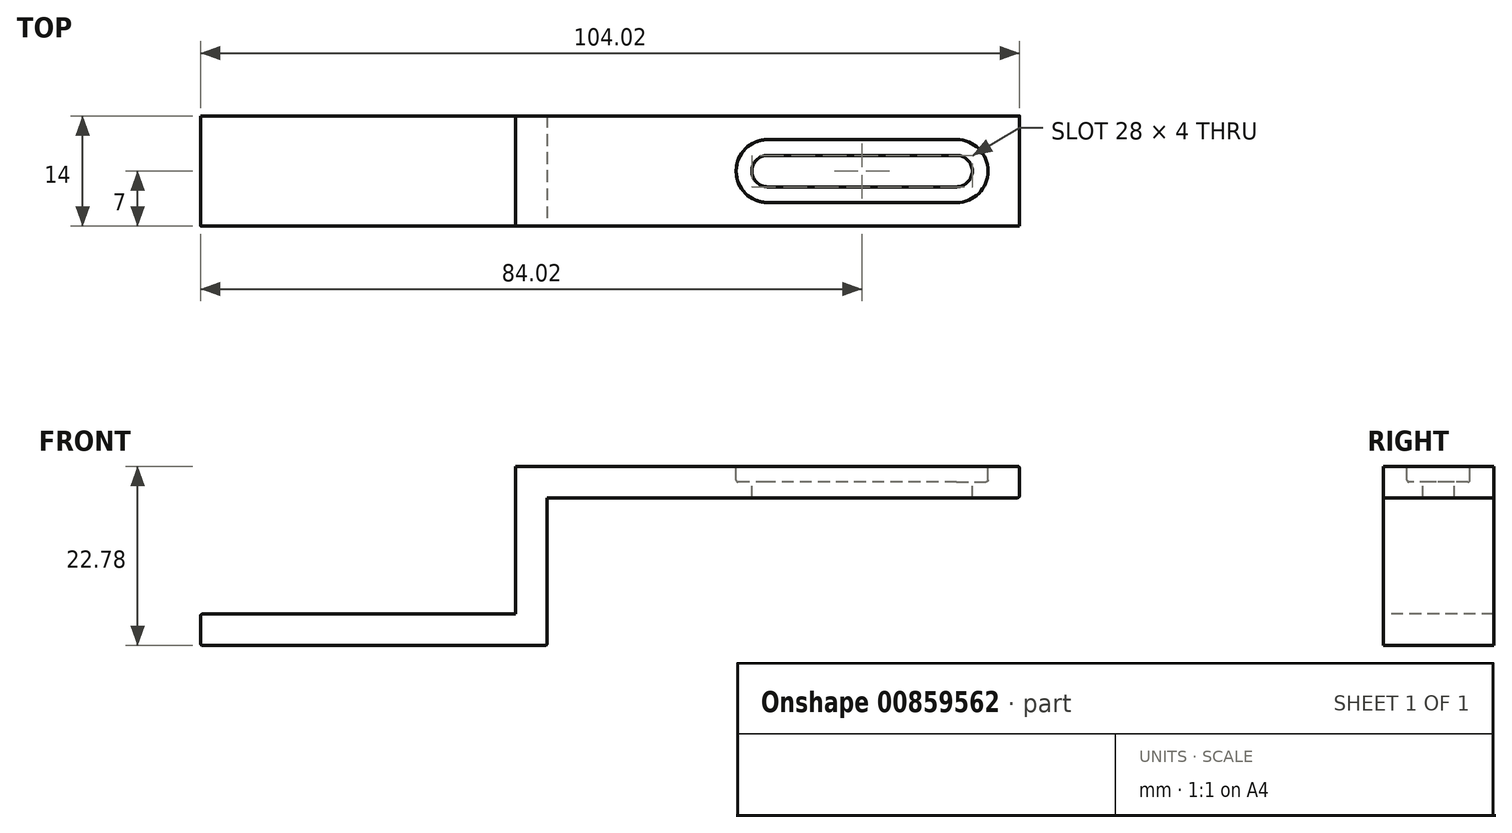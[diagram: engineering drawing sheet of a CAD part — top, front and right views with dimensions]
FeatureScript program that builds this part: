
annotation { "Feature Type Name" : "Feature", "Feature Type Description" : "" }
export const myFeature = defineFeature(function(context is Context, id is Id, definition is map)
    precondition{}
    {
        {
            var Q0;
            Q0=qCreatedBy(makeId("Top.planeOp"),FACE);
            var sketch = newSketch(context, id + "F0", { "sketchPlane" : qUnion([Q0])});
            skLineSegment(sketch, "E0.bottom", {"start": v(43, -7) * mm, "end": v(-43, -7) * mm});
            skLineSegment(sketch, "E0.top", {"start": v(43, 7) * mm, "end": v(-43, 7) * mm});
            skLineSegment(sketch, "E0.left", {"start": v(43, -7) * mm, "end": v(43, 7) * mm});
            skLineSegment(sketch, "E0.right", {"start": v(-43, -7) * mm, "end": v(-43, 7) * mm});
            skPoint(sketch, "E0.middle", {"position": v(0, 0) * mm});
            skSolve(sketch);
        }
        {
            var Q0;
            Q0=qSketchRegion(id+"F0",true);
            extrude(context, id + "F1", {"entities" : qUnion([Q0]), "depth" : 4 * mm, "offsetDistance" : 25.4 * mm});
        }
        {
            var Q0;
            Q0=makeQuery(id+"F1.opExtrude","CAP_FACE",FACE,{"disambiguationData":[OSD([sQuery(id+"F0.wireOp",EDGE,"E0.bottom"),sQuery(id+"F0.wireOp",EDGE,"E0.top"),sQuery(id+"F0.wireOp",EDGE,"E0.left"),sQuery(id+"F0.wireOp",EDGE,"E0.right")])],"isStart":false});
            var sketch = newSketch(context, id + "F2", { "sketchPlane" : qUnion([Q0])});
            skLineSegment(sketch, "E1", {"start": v(-43, 0) * mm, "end": v(43, 0) * mm, "construction": true});
            skCircle(sketch, "E2", {"center": v(35, 0) * mm, "radius": 2 * mm});
            skCircle(sketch, "E3", {"center": v(11, 0) * mm, "radius": 2 * mm});
            skLineSegment(sketch, "E4.bottom", {"start": v(11, -2) * mm, "end": v(35, -2) * mm});
            skLineSegment(sketch, "E4.top", {"start": v(11, 2) * mm, "end": v(35, 2) * mm});
            skLineSegment(sketch, "E4.left", {"start": v(11, -2) * mm, "end": v(11, 2) * mm});
            skLineSegment(sketch, "E4.right", {"start": v(35, -2) * mm, "end": v(35, 2) * mm});
            skSolve(sketch);
        }
        {
            var Q0;
            Q0=qSketchRegion(id+"F2",true);
            extrude(context, id + "F3", {"entities" : qUnion([Q0]), "operationType" : NewBodyOperationType.REMOVE, "oppositeDirection" : true, "depth" : 4 * mm, "offsetDistance" : 25.4 * mm});
        }
        {
            var Q0;
            Q0=makeQuery(id+"F1.opExtrude","CAP_FACE",FACE,{"disambiguationData":[OSD([sQuery(id+"F0.wireOp",EDGE,"E0.bottom"),sQuery(id+"F0.wireOp",EDGE,"E0.top"),sQuery(id+"F0.wireOp",EDGE,"E0.left"),sQuery(id+"F0.wireOp",EDGE,"E0.right")])],"isStart":false});
            var sketch = newSketch(context, id + "F4", { "sketchPlane" : qUnion([Q0])});
            skLineSegment(sketch, "E5", {"start": v(-43, 0) * mm, "end": v(43, 0) * mm, "construction": true});
            skCircle(sketch, "E6", {"center": v(35, 0) * mm, "radius": 4 * mm});
            skCircle(sketch, "E7", {"center": v(11, 0) * mm, "radius": 4 * mm});
            skLineSegment(sketch, "E8.bottom", {"start": v(11, -4) * mm, "end": v(35, -4) * mm});
            skLineSegment(sketch, "E8.top", {"start": v(11, 4) * mm, "end": v(35, 4) * mm});
            skLineSegment(sketch, "E8.left", {"start": v(11, -4) * mm, "end": v(11, 4) * mm});
            skLineSegment(sketch, "E8.right", {"start": v(35, -4) * mm, "end": v(35, 4) * mm});
            skSolve(sketch);
        }
        {
            var Q0;
            Q0=qSketchRegion(id+"F4",true);
            extrude(context, id + "F5", {"entities" : qUnion([Q0]), "operationType" : NewBodyOperationType.REMOVE, "oppositeDirection" : true, "depth" : 2 * mm, "offsetDistance" : 25.4 * mm});
        }
        {
            var Q0;
            Q0=makeQuery(id+"F5.boolean.opBoolean","COPY",EDGE,{"derivedFrom":makeQuery(id+"F5.opExtrude","CAP_EDGE",EDGE,{"disambiguationData":[OSD([sQuery(id+"F4.wireOp",EDGE,"E8.top")])],"isStart":false})});
            var Q1;
            Q1=makeQuery(id+"F5.boolean.opBoolean","COPY",EDGE,{"derivedFrom":makeQuery(id+"F5.opExtrude","CAP_EDGE",EDGE,{"disambiguationData":[OSD([sQuery(id+"F4.wireOp",EDGE,"E7")])],"isStart":false})});
            var Q2;
            Q2=makeQuery(id+"F5.boolean.opBoolean","COPY",EDGE,{"derivedFrom":makeQuery(id+"F5.opExtrude","CAP_EDGE",EDGE,{"disambiguationData":[OSD([sQuery(id+"F4.wireOp",EDGE,"E8.bottom")])],"isStart":false})});
            var Q3;
            Q3=makeQuery(id+"F5.boolean.opBoolean","COPY",EDGE,{"derivedFrom":makeQuery(id+"F5.opExtrude","CAP_EDGE",EDGE,{"disambiguationData":[OSD([sQuery(id+"F4.wireOp",EDGE,"E6")])],"isStart":false})});
            var Q4;
            Q4=makeQuery(id+"F5.boolean.opBoolean","COPY",EDGE,{"derivedFrom":makeQuery(id+"F5.opExtrude","CAP_EDGE",EDGE,{"disambiguationData":[OSD([sQuery(id+"F4.wireOp",EDGE,"E8.bottom")])],"isStart":true})});
            var Q5;
            Q5=makeQuery(id+"F5.boolean.opBoolean","COPY",EDGE,{"derivedFrom":makeQuery(id+"F5.opExtrude","CAP_EDGE",EDGE,{"disambiguationData":[OSD([sQuery(id+"F4.wireOp",EDGE,"E7")])],"isStart":true})});
            var Q6;
            Q6=makeQuery(id+"F5.boolean.opBoolean","COPY",EDGE,{"derivedFrom":makeQuery(id+"F5.opExtrude","CAP_EDGE",EDGE,{"disambiguationData":[OSD([sQuery(id+"F4.wireOp",EDGE,"E8.top")])],"isStart":true})});
            var Q7;
            Q7=makeQuery(id+"F5.boolean.opBoolean","COPY",EDGE,{"derivedFrom":makeQuery(id+"F5.opExtrude","CAP_EDGE",EDGE,{"disambiguationData":[OSD([sQuery(id+"F4.wireOp",EDGE,"E6")])],"isStart":true})});
            fillet(context, id + "F6", {"entities" : qUnion([Q0, Q1, Q2, Q3, Q4, Q5, Q6, Q7]), "radius" : 0.25 * mm, "tangentPropagation" : true, "allowEdgeOverflow" : false});
        }
        {
            var Q0;
            Q0=makeQuery(id+"F1.opExtrude","CAP_FACE",FACE,{"disambiguationData":[OSD([sQuery(id+"F0.wireOp",EDGE,"E0.bottom"),sQuery(id+"F0.wireOp",EDGE,"E0.top"),sQuery(id+"F0.wireOp",EDGE,"E0.left"),sQuery(id+"F0.wireOp",EDGE,"E0.right")])],"isStart":false});
            var sketch = newSketch(context, id + "F7", { "sketchPlane" : qUnion([Q0])});
            skLineSegment(sketch, "E9.bottom", {"start": v(-43, -7) * mm, "end": v(-21.02, -7) * mm});
            skLineSegment(sketch, "E9.top", {"start": v(-43, 7) * mm, "end": v(-21.02, 7) * mm});
            skLineSegment(sketch, "E9.left", {"start": v(-43, -7) * mm, "end": v(-43, 7) * mm});
            skLineSegment(sketch, "E9.right", {"start": v(-21.02, -7) * mm, "end": v(-21.02, 7) * mm});
            skSolve(sketch);
        }
        {
            var Q0;
            Q0=makeQuery(id+"F7.imprint","IMPRINT",FACE,{"disambiguationData":[TD([[makeQuery(id+"F7.imprint","IMPRINT",EDGE,{"derivedFrom":sQuery(id+"F7.wireOp",EDGE,"E9.bottom")}),-1.0]])]});
            extrude(context, id + "F8", {"entities" : qUnion([Q0]), "operationType" : NewBodyOperationType.REMOVE, "oppositeDirection" : true, "depth" : 4 * mm, "offsetDistance" : 25.4 * mm});
        }
        {
            var Q0;
            Q0=makeQuery(id+"F1.opExtrude","CAP_FACE",FACE,{"disambiguationData":[OSD([sQuery(id+"F0.wireOp",EDGE,"E0.bottom"),sQuery(id+"F0.wireOp",EDGE,"E0.top"),sQuery(id+"F0.wireOp",EDGE,"E0.left"),sQuery(id+"F0.wireOp",EDGE,"E0.right")])],"isStart":true});
            var sketch = newSketch(context, id + "F9", { "sketchPlane" : qUnion([Q0])});
            skLineSegment(sketch, "E10.bottom", {"start": v(-21.02, -7) * mm, "end": v(-17.02, -7) * mm});
            skLineSegment(sketch, "E10.top", {"start": v(-21.02, 7) * mm, "end": v(-17.02, 7) * mm});
            skLineSegment(sketch, "E10.left", {"start": v(-21.02, -7) * mm, "end": v(-21.02, 7) * mm});
            skLineSegment(sketch, "E10.right", {"start": v(-17.02, -7) * mm, "end": v(-17.02, 7) * mm});
            skSolve(sketch);
        }
        {
            var Q0;
            Q0 = qSketchRegion(id + "F9", true);
            extrude(context, id + "F10", {"entities" : qUnion([Q0]), "operationType" : NewBodyOperationType.ADD, "depth" : 18.78 * mm, "offsetDistance" : 25.4 * mm});
        }
        {
            var Q0;
            Q0=makeQuery(id+"F10.boolean.opBoolean","MERGE",FACE,{"derivedFrom":[makeQuery(id+"F8.boolean.opBoolean","COPY",FACE,{"derivedFrom":makeQuery(id+"F8.opExtrude","SWEPT_FACE",FACE,{"disambiguationData":[OSD([sQuery(id+"F7.wireOp",EDGE,"E9.right")])]})}),makeQuery(id+"F10.opExtrude","SWEPT_FACE",FACE,{"disambiguationData":[OSD([sQuery(id+"F9.wireOp",EDGE,"E10.left")])]})]});
            var sketch = newSketch(context, id + "F11", { "sketchPlane" : qUnion([Q0])});
            skLineSegment(sketch, "E11.bottom", {"start": v(-7, -18.78) * mm, "end": v(7, -18.78) * mm});
            skLineSegment(sketch, "E11.top", {"start": v(-7, -14.78) * mm, "end": v(7, -14.78) * mm});
            skLineSegment(sketch, "E11.left", {"start": v(-7, -18.78) * mm, "end": v(-7, -14.78) * mm});
            skLineSegment(sketch, "E11.right", {"start": v(7, -18.78) * mm, "end": v(7, -14.78) * mm});
            skSolve(sketch);
        }
        {
            var Q0;
            Q0 = qSketchRegion(id + "F11", true);
            extrude(context, id + "F12", {"entities" : qUnion([Q0]), "operationType" : NewBodyOperationType.ADD, "depth" : 40 * mm, "offsetDistance" : 25.4 * mm});
        }
        {
            var Q0;
            Q0=makeQuery(id+"F10.opExtrude","CAP_EDGE",EDGE,{"disambiguationData":[OSD([sQuery(id+"F9.wireOp",EDGE,"E10.right")])],"isStart":true});
            var Q1;
            Q1=makeQuery(id+"F10.opExtrude","CAP_EDGE",EDGE,{"disambiguationData":[OSD([sQuery(id+"F9.wireOp",EDGE,"E10.right")])],"isStart":false});
            var Q2;
            Q2=makeQuery(id+"F1.opExtrude","CAP_EDGE",EDGE,{"disambiguationData":[OSD([sQuery(id+"F0.wireOp",EDGE,"E0.left")])],"isStart":true});
            var Q3;
            Q3=makeQuery(id+"F1.opExtrude","CAP_EDGE",EDGE,{"disambiguationData":[OSD([sQuery(id+"F0.wireOp",EDGE,"E0.left")])],"isStart":false});
            var Q4;
            Q4=makeQuery(id+"F12.opExtrude","CAP_EDGE",EDGE,{"disambiguationData":[OSD([sQuery(id+"F11.wireOp",EDGE,"E11.top")])],"isStart":true});
            var Q5;
            Q5=makeQuery(id+"F8.boolean.opBoolean","COPY",EDGE,{"derivedFrom":makeQuery(id+"F8.opExtrude","CAP_EDGE",EDGE,{"disambiguationData":[OSD([sQuery(id+"F7.wireOp",EDGE,"E9.right")])],"isStart":true})});
            var Q6;
            Q6=makeQuery(id+"F12.opExtrude","CAP_EDGE",EDGE,{"disambiguationData":[OSD([sQuery(id+"F11.wireOp",EDGE,"E11.top")])],"isStart":false});
            var Q7;
            Q7=makeQuery(id+"F12.opExtrude","CAP_EDGE",EDGE,{"disambiguationData":[OSD([sQuery(id+"F11.wireOp",EDGE,"E11.bottom")])],"isStart":false});
            fillet(context, id + "F13", {"entities" : qUnion([Q0, Q1, Q2, Q3, Q4, Q5, Q6, Q7]), "radius" : 0.25 * mm, "tangentPropagation" : true, "allowEdgeOverflow" : false});
        }
    });
